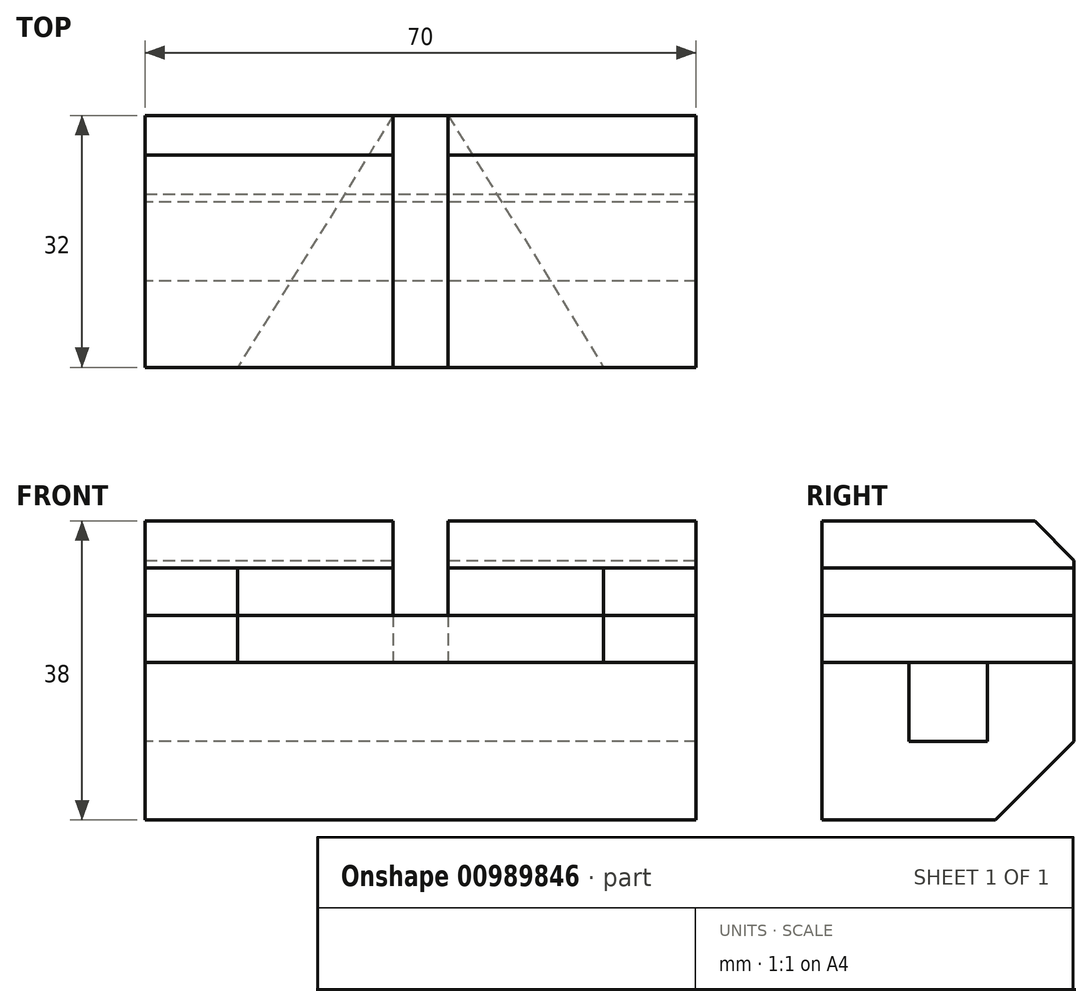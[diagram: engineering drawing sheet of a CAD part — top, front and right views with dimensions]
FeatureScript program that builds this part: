
annotation { "Feature Type Name" : "Feature", "Feature Type Description" : "" }
export const myFeature = defineFeature(function(context is Context, id is Id, definition is map)
    precondition{}
    {
        {
            var Q0;
            Q0=qCreatedBy(makeId("Top.planeOp"),FACE);
            var sketch = newSketch(context, id + "F0", { "sketchPlane" : qUnion([Q0])});
            skLineSegment(sketch, "E0.bottom", {"start": v(35, -16) * mm, "end": v(-35, -16) * mm});
            skLineSegment(sketch, "E0.top", {"start": v(35, 16) * mm, "end": v(-35, 16) * mm});
            skLineSegment(sketch, "E0.left", {"start": v(35, -16) * mm, "end": v(35, 16) * mm});
            skLineSegment(sketch, "E0.right", {"start": v(-35, -16) * mm, "end": v(-35, 16) * mm});
            skPoint(sketch, "E0.middle", {"position": v(0, 0) * mm});
            skLineSegment(sketch, "E1", {"start": v(-3.5, 16) * mm, "end": v(3.5, 16) * mm});
            skLineSegment(sketch, "E2", {"start": v(-23.25, -16) * mm, "end": v(23.25, -16) * mm});
            skLineSegment(sketch, "E3", {"start": v(-3.5, 16) * mm, "end": v(-23.25, -16) * mm});
            skLineSegment(sketch, "E4", {"start": v(3.5, 16) * mm, "end": v(23.25, -16) * mm});
            skSolve(sketch);
        }
        {
            var Q0;
            {var subQ0=sQuery(id+"F0.wireOp",EDGE,"E0.right");Q0=makeQuery(id+"F0.imprint","IMPRINT",FACE,{"disambiguationData":[TD([[makeQuery(id+"F0.imprint","IMPRINT",EDGE,{"derivedFrom":subQ0}),-1.0]])]});}
            var Q1;
            {var subQ0=sQuery(id+"F0.wireOp",EDGE,"E0.left");Q1=makeQuery(id+"F0.imprint","IMPRINT",FACE,{"disambiguationData":[TD([[makeQuery(id+"F0.imprint","IMPRINT",EDGE,{"derivedFrom":subQ0}),1.0]])]});}
            extrude(context, id + "F1", {"entities" : qUnion([Q0, Q1]), "depth" : 12 * mm, "offsetDistance" : 25 * mm});
        }
        {
            var Q0;
            Q0 = qSketchRegion(id + "F0", true);
            extrude(context, id + "F2", {"entities" : qUnion([Q0]), "depth" : 6 * mm, "offsetDistance" : 25 * mm});
        }
        {
            var Q0;
            Q0=qCreatedBy(makeId("Front.planeOp"),FACE);
            var sketch = newSketch(context, id + "F3", { "sketchPlane" : qUnion([Q0])});
            skLineSegment(sketch, "E5.bottom", {"start": v(-35, 12) * mm, "end": v(-3.5, 12) * mm});
            skLineSegment(sketch, "E5.top", {"start": v(-35, 18) * mm, "end": v(-3.5, 18) * mm});
            skLineSegment(sketch, "E5.left", {"start": v(-35, 12) * mm, "end": v(-35, 18) * mm});
            skLineSegment(sketch, "E5.right", {"start": v(-3.5, 12) * mm, "end": v(-3.5, 18) * mm});
            skLineSegment(sketch, "E6.bottom", {"start": v(35, 12) * mm, "end": v(3.5, 12) * mm});
            skLineSegment(sketch, "E6.top", {"start": v(35, 18) * mm, "end": v(3.5, 18) * mm});
            skLineSegment(sketch, "E6.left", {"start": v(35, 12) * mm, "end": v(35, 18) * mm});
            skLineSegment(sketch, "E6.right", {"start": v(3.5, 12) * mm, "end": v(3.5, 18) * mm});
            skSolve(sketch);
        }
        {
            var Q0;
            Q0=makeQuery(id+"F3.imprint","IMPRINT",FACE,{"disambiguationData":[TD([[makeQuery(id+"F3.imprint","IMPRINT",EDGE,{"derivedFrom":sQuery(id+"F3.wireOp",EDGE,"E5.bottom")}),1.0]])]});
            var Q1;
            Q1=makeQuery(id+"F3.imprint","IMPRINT",FACE,{"disambiguationData":[TD([[makeQuery(id+"F3.imprint","IMPRINT",EDGE,{"derivedFrom":sQuery(id+"F3.wireOp",EDGE,"E6.bottom")}),-1.0]])]});
            extrude(context, id + "F4", {"entities" : qUnion([Q0, Q1]), "endBound" : BoundingType.SYMMETRIC, "depth" : 32 * mm, "offsetDistance" : 25 * mm});
        }
        {
            var Q0;
            Q0=makeQuery(id+"F4.opExtrude","CAP_EDGE",EDGE,{"disambiguationData":[OSD([sQuery(id+"F3.wireOp",EDGE,"E5.top")])],"isStart":true});
            var Q1;
            Q1=makeQuery(id+"F4.opExtrude","CAP_EDGE",EDGE,{"disambiguationData":[OSD([sQuery(id+"F3.wireOp",EDGE,"E6.top")])],"isStart":true});
            chamfer(context, id + "F5", {"entities" : qUnion([Q0, Q1]), "width" : 5 * mm, "tangentPropagation" : true});
        }
        {
            var Q0;
            Q0=qCreatedBy(makeId("Right.planeOp"),FACE);
            var sketch = newSketch(context, id + "F6", { "sketchPlane" : qUnion([Q0])});
            skLineSegment(sketch, "E7.bottom", {"start": v(-16, 0) * mm, "end": v(16, 0) * mm});
            skLineSegment(sketch, "E7.top", {"start": v(-16, -20) * mm, "end": v(16, -20) * mm});
            skLineSegment(sketch, "E7.left", {"start": v(-16, 0) * mm, "end": v(-16, -20) * mm});
            skLineSegment(sketch, "E7.right", {"start": v(16, 0) * mm, "end": v(16, -20) * mm});
            skLineSegment(sketch, "E8.bottom", {"start": v(-5, 0) * mm, "end": v(5, 0) * mm});
            skLineSegment(sketch, "E8.top", {"start": v(-5, -10) * mm, "end": v(5, -10) * mm});
            skLineSegment(sketch, "E8.left", {"start": v(-5, 0) * mm, "end": v(-5, -10) * mm});
            skLineSegment(sketch, "E8.right", {"start": v(5, 0) * mm, "end": v(5, -10) * mm});
            skSolve(sketch);
        }
        {
            var Q0;
            Q0=makeQuery(id+"F6.imprint","IMPRINT",FACE,{"disambiguationData":[TD([[makeQuery(id+"F6.imprint","IMPRINT",EDGE,{"derivedFrom":sQuery(id+"F6.wireOp",EDGE,"E7.top")}),1.0]])]});
            extrude(context, id + "F7", {"entities" : qUnion([Q0]), "endBound" : BoundingType.SYMMETRIC, "depth" : 70 * mm, "offsetDistance" : 25 * mm});
        }
        {
            var Q0;
            Q0=makeQuery(id+"F7.opExtrude","SWEPT_EDGE",EDGE,{"disambiguationData":[OSD([sQuery(id+"F6.wireOp",EDGE,"E7.top"),sQuery(id+"F6.wireOp",EDGE,"E7.right")])]});
            chamfer(context, id + "F8", {"entities" : qUnion([Q0]), "width" : 10 * mm, "tangentPropagation" : true});
        }
    });
